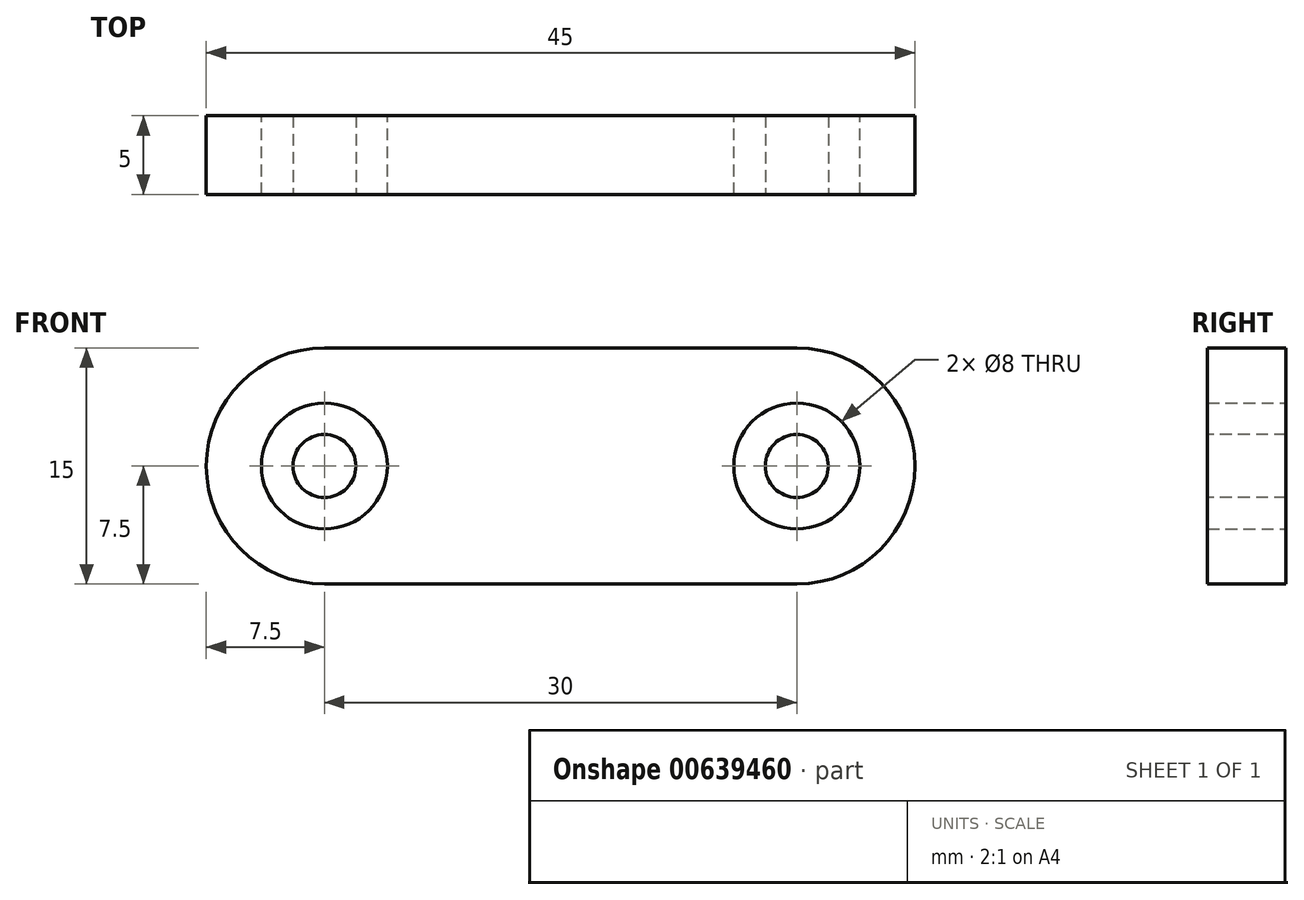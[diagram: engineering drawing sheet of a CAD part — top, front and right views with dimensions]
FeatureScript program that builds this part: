
annotation { "Feature Type Name" : "Feature", "Feature Type Description" : "" }
export const myFeature = defineFeature(function(context is Context, id is Id, definition is map)
    precondition{}
    {
        {
            var Q0;
            Q0=qCreatedBy(makeId("Front.planeOp"),FACE);
            var sketch = newSketch(context, id + "F0", { "sketchPlane" : qUnion([Q0])});
            skArc(sketch, "E0", {"start": v(0, 7.5) * mm, "mid": v(-7.5, 0) * mm, "end": v(0, -7.5) * mm});
            skArc(sketch, "E1", {"start": v(30, -7.5) * mm, "mid": v(37.5, 0) * mm, "end": v(30, 7.5) * mm});
            skLineSegment(sketch, "E2", {"start": v(0, 0) * mm, "end": v(30, 0) * mm});
            skLineSegment(sketch, "E3", {"start": v(0, 7.5) * mm, "end": v(30, 7.5) * mm});
            skLineSegment(sketch, "E4", {"start": v(0, -7.5) * mm, "end": v(30, -7.5) * mm});
            skCircle(sketch, "E5", {"center": v(0, 0) * mm, "radius": 4 * mm});
            skCircle(sketch, "E6", {"center": v(30, 0) * mm, "radius": 4 * mm});
            skSolve(sketch);
        }
        {
            var Q0;
            Q0=makeQuery(id+"F0.imprint","IMPRINT",FACE,{"disambiguationData":[TD([[makeQuery(id+"F0.imprint","IMPRINT",EDGE,{"derivedFrom":sQuery(id+"F0.wireOp",EDGE,"E0")}),1.0]])]});
            extrude(context, id + "F1", {"entities" : qUnion([Q0]), "depth" : 5 * mm, "offsetDistance" : 25.4 * mm});
        }
        {
            var Q0;
            Q0=makeQuery(id+"F1.opExtrude","CAP_FACE",FACE,{"disambiguationData":[OSD([sQuery(id+"F0.wireOp",EDGE,"E0"),sQuery(id+"F0.wireOp",EDGE,"E1"),sQuery(id+"F0.wireOp",EDGE,"E3"),sQuery(id+"F0.wireOp",EDGE,"E4"),sQuery(id+"F0.wireOp",EDGE,"E5"),sQuery(id+"F0.wireOp",EDGE,"E6")])],"isStart":false});
            var sketch = newSketch(context, id + "F2", { "sketchPlane" : qUnion([Q0])});
            skCircle(sketch, "E7", {"center": v(0, 0) * mm, "radius": 2 * mm});
            skCircle(sketch, "E8", {"center": v(30, 0) * mm, "radius": 2 * mm});
            skSolve(sketch);
        }
        {
            var Q0;
            Q0=makeQuery(id+"F2.imprint","IMPRINT",FACE,{"disambiguationData":[TD([[makeQuery(id+"F2.imprint","IMPRINT",EDGE,{"derivedFrom":sQuery(id+"F2.wireOp",EDGE,"E8")}),1.0]])]});
            var Q1;
            Q1=makeQuery(id+"F2.imprint","IMPRINT",FACE,{"disambiguationData":[TD([[makeQuery(id+"F2.imprint","IMPRINT",EDGE,{"derivedFrom":sQuery(id+"F2.wireOp",EDGE,"E7")}),1.0]])]});
            extrude(context, id + "F3", {"entities" : qUnion([Q0, Q1]), "oppositeDirection" : true, "depth" : 5 * mm, "offsetDistance" : 25.4 * mm});
        }
    });
